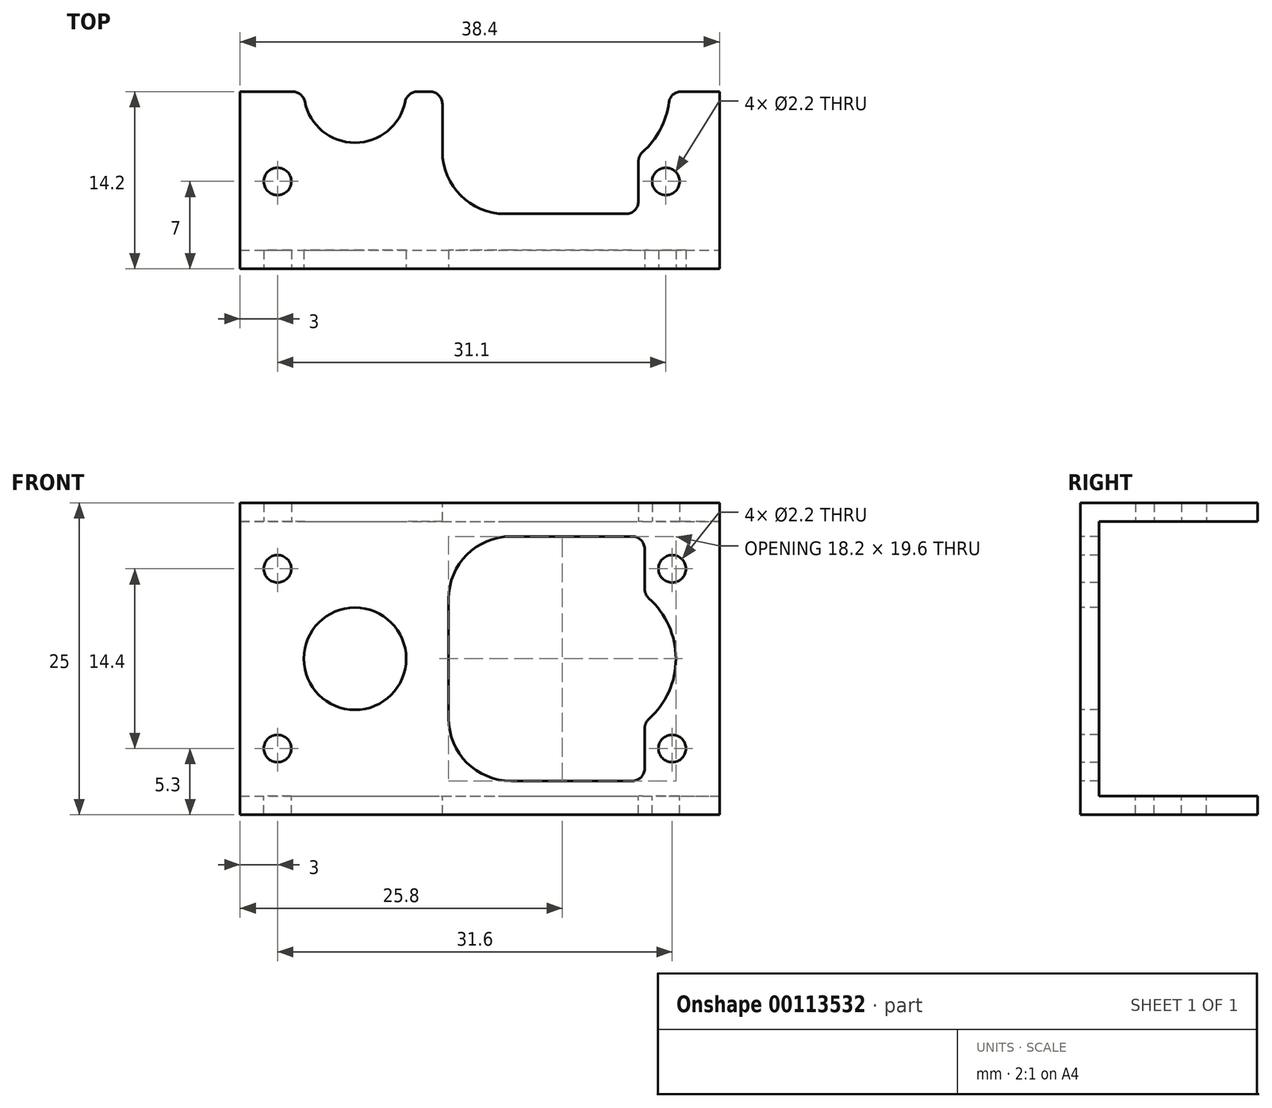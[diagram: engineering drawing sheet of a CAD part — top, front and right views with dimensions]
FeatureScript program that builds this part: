
annotation { "Feature Type Name" : "Feature", "Feature Type Description" : "" }
export const myFeature = defineFeature(function(context is Context, id is Id, definition is map)
    precondition{}
    {
        {
            var Q0;
            Q0=qCreatedBy(makeId("Top.planeOp"),FACE);
            var sketch = newSketch(context, id + "F0", { "sketchPlane" : qUnion([Q0])});
            skLineSegment(sketch, "E0.bottom", {"start": v(19.2, -14.2) * mm, "end": v(-19.2, -14.2) * mm});
            skLineSegment(sketch, "E0.top", {"start": v(19.2, 14.2) * mm, "end": v(-19.2, 14.2) * mm});
            skLineSegment(sketch, "E0.left", {"start": v(19.2, -14.2) * mm, "end": v(19.2, 14.2) * mm});
            skLineSegment(sketch, "E0.right", {"start": v(-19.2, -14.2) * mm, "end": v(-19.2, 14.2) * mm});
            skPoint(sketch, "E0.middle", {"position": v(0, 0) * mm});
            skCircle(sketch, "E1", {"center": v(-10, 0) * mm, "radius": 4.1 * mm});
            skCircle(sketch, "E2", {"center": v(-16.2, 7.2) * mm, "radius": 1.1 * mm});
            skCircle(sketch, "E3", {"center": v(14.9, 7.2) * mm, "radius": 1.1 * mm});
            skLineSegment(sketch, "E4.bottom", {"start": v(2, 9.8) * mm, "end": v(11.7, 9.8) * mm});
            skLineSegment(sketch, "E4.top", {"start": v(2, -9.8) * mm, "end": v(11.7, -9.8) * mm});
            skLineSegment(sketch, "E4.left", {"start": v(-3, 4.8) * mm, "end": v(-3, -4.8) * mm});
            skLineSegment(sketch, "E4.right", {"start": v(12.7, 8.8) * mm, "end": v(12.7, 5.6) * mm});
            skPoint(sketch, "E4.middle", {"position": v(4.85, 0) * mm});
            skPoint(sketch, "E5.visualSharp", {"position": v(-3, 9.8) * mm});
            skArc(sketch, "E5.filletArc", {"start": v(2, 9.8) * mm, "mid": v(-1.54, 8.34) * mm, "end": v(-3, 4.8) * mm});
            skPoint(sketch, "E6.visualSharp", {"position": v(-3, -9.8) * mm});
            skArc(sketch, "E6.filletArc", {"start": v(-3, -4.8) * mm, "mid": v(-1.54, -8.34) * mm, "end": v(2, -9.8) * mm});
            skPoint(sketch, "E7.visualSharp", {"position": v(12.7, 9.8) * mm});
            skArc(sketch, "E7.filletArc", {"start": v(12.7, 8.8) * mm, "mid": v(12.4, 9.5) * mm, "end": v(11.7, 9.8) * mm});
            skPoint(sketch, "E8.visualSharp", {"position": v(12.7, -9.8) * mm});
            skArc(sketch, "E8.filletArc", {"start": v(11.7, -9.8) * mm, "mid": v(12.4, -9.5) * mm, "end": v(12.7, -8.8) * mm});
            skCircle(sketch, "E9.MirrorC", {"center": v(-16.2, -7.2) * mm, "radius": 1.1 * mm});
            skCircle(sketch, "E10.MirrorC", {"center": v(14.9, -7.2) * mm, "radius": 1.1 * mm});
            skArc(sketch, "E11", {"start": v(13.03, -4.84) * mm, "mid": v(15.2, 0) * mm, "end": v(13.03, 4.84) * mm});
            skLineSegment(sketch, "E12.trimOffspring", {"start": v(12.7, -5.6) * mm, "end": v(12.7, -8.8) * mm});
            skPoint(sketch, "E13.visualSharp", {"position": v(12.7, 5.12) * mm});
            skArc(sketch, "E13.filletArc", {"start": v(12.7, 5.6) * mm, "mid": v(12.79, 5.18) * mm, "end": v(13.03, 4.84) * mm});
            skPoint(sketch, "E14.visualSharp", {"position": v(12.7, -5.12) * mm});
            skArc(sketch, "E14.filletArc", {"start": v(13.03, -4.84) * mm, "mid": v(12.79, -5.18) * mm, "end": v(12.7, -5.6) * mm});
            skSolve(sketch);
        }
        {
            var Q0;
            Q0=qSketchRegion(id+"F0",true);
            extrude(context, id + "F1", {"entities" : qUnion([Q0]), "depth" : 1.5 * mm});
        }
        {
            var Q0;
            Q0=makeQuery(id+"F1.opExtrude","CAP_FACE",FACE,{"disambiguationData":[OSD([sQuery(id+"F0.wireOp",EDGE,"E0.bottom"),sQuery(id+"F0.wireOp",EDGE,"E0.top"),sQuery(id+"F0.wireOp",EDGE,"E0.left"),sQuery(id+"F0.wireOp",EDGE,"E0.right"),sQuery(id+"F0.wireOp",EDGE,"E1"),sQuery(id+"F0.wireOp",EDGE,"E2"),sQuery(id+"F0.wireOp",EDGE,"E3"),sQuery(id+"F0.wireOp",EDGE,"E4.bottom"),sQuery(id+"F0.wireOp",EDGE,"E4.top"),sQuery(id+"F0.wireOp",EDGE,"E4.left"),sQuery(id+"F0.wireOp",EDGE,"E4.right"),sQuery(id+"F0.wireOp",EDGE,"E5.filletArc"),sQuery(id+"F0.wireOp",EDGE,"E6.filletArc"),sQuery(id+"F0.wireOp",EDGE,"E7.filletArc"),sQuery(id+"F0.wireOp",EDGE,"E8.filletArc"),sQuery(id+"F0.wireOp",EDGE,"E9.MirrorC"),sQuery(id+"F0.wireOp",EDGE,"E10.MirrorC"),sQuery(id+"F0.wireOp",EDGE,"E11"),sQuery(id+"F0.wireOp",EDGE,"E12.trimOffspring"),sQuery(id+"F0.wireOp",EDGE,"E13.filletArc"),sQuery(id+"F0.wireOp",EDGE,"E14.filletArc")])],"isStart":true});
            var sketch = newSketch(context, id + "F2", { "sketchPlane" : qUnion([Q0])});
            skLineSegment(sketch, "E15.bottom", {"start": v(-19.2, 14.2) * mm, "end": v(19.2, 14.2) * mm});
            skLineSegment(sketch, "E15.top", {"start": v(-19.2, 12.7) * mm, "end": v(19.2, 12.7) * mm});
            skLineSegment(sketch, "E15.left", {"start": v(-19.2, 14.2) * mm, "end": v(-19.2, 12.7) * mm});
            skLineSegment(sketch, "E15.right", {"start": v(19.2, 14.2) * mm, "end": v(19.2, 12.7) * mm});
            skSolve(sketch);
        }
        {
            var Q0;
            Q0=qSketchRegion(id+"F2",true);
            extrude(context, id + "F3", {"entities" : qUnion([Q0]), "operationType" : NewBodyOperationType.ADD, "depth" : 11 * mm});
        }
        {
            var Q0;
            Q0=qCreatedBy(makeId("Top.planeOp"),FACE);
            cPlane(context, id + "F4", {"entities" : qUnion([Q0]), "cplaneType" : CPlaneType.OFFSET, "offset" : 11 * mm, "oppositeDirection" : true, "width" : 150 * mm, "height" : 150 * mm});
        }
        {
            var Q0;
            Q0=makeQuery(id+"F1.opExtrude","SWEPT_BODY",BODY,{"disambiguationData":[OSD([sQuery(id+"F0.wireOp",EDGE,"E0.bottom"),sQuery(id+"F0.wireOp",EDGE,"E0.top"),sQuery(id+"F0.wireOp",EDGE,"E0.left"),sQuery(id+"F0.wireOp",EDGE,"E0.right"),sQuery(id+"F0.wireOp",EDGE,"E1"),sQuery(id+"F0.wireOp",EDGE,"E2"),sQuery(id+"F0.wireOp",EDGE,"E3"),sQuery(id+"F0.wireOp",EDGE,"E4.bottom"),sQuery(id+"F0.wireOp",EDGE,"E4.top"),sQuery(id+"F0.wireOp",EDGE,"E4.left"),sQuery(id+"F0.wireOp",EDGE,"E4.right"),sQuery(id+"F0.wireOp",EDGE,"E5.filletArc"),sQuery(id+"F0.wireOp",EDGE,"E6.filletArc"),sQuery(id+"F0.wireOp",EDGE,"E7.filletArc"),sQuery(id+"F0.wireOp",EDGE,"E8.filletArc"),sQuery(id+"F0.wireOp",EDGE,"E9.MirrorC"),sQuery(id+"F0.wireOp",EDGE,"E10.MirrorC"),sQuery(id+"F0.wireOp",EDGE,"E11"),sQuery(id+"F0.wireOp",EDGE,"E12.trimOffspring"),sQuery(id+"F0.wireOp",EDGE,"E13.filletArc"),sQuery(id+"F0.wireOp",EDGE,"E14.filletArc")])]});
            var Q1;
            Q1=qCreatedBy(id+"F4.planeOp",FACE);
            mirror(context, id + "F5", {"operationType" : NewBodyOperationType.ADD, "entities" : qUnion([Q0]), "mirrorPlane" : qUnion([Q1])});
        }
        {
            var Q0;
            Q0=makeQuery(id+"F5.opPattern","COPY",FACE,{"derivedFrom":makeQuery(id+"F1.opExtrude","CAP_FACE",FACE,{"disambiguationData":[OSD([sQuery(id+"F0.wireOp",EDGE,"E0.bottom"),sQuery(id+"F0.wireOp",EDGE,"E0.top"),sQuery(id+"F0.wireOp",EDGE,"E0.left"),sQuery(id+"F0.wireOp",EDGE,"E0.right"),sQuery(id+"F0.wireOp",EDGE,"E1"),sQuery(id+"F0.wireOp",EDGE,"E2"),sQuery(id+"F0.wireOp",EDGE,"E3"),sQuery(id+"F0.wireOp",EDGE,"E4.bottom"),sQuery(id+"F0.wireOp",EDGE,"E4.top"),sQuery(id+"F0.wireOp",EDGE,"E4.left"),sQuery(id+"F0.wireOp",EDGE,"E4.right"),sQuery(id+"F0.wireOp",EDGE,"E5.filletArc"),sQuery(id+"F0.wireOp",EDGE,"E6.filletArc"),sQuery(id+"F0.wireOp",EDGE,"E7.filletArc"),sQuery(id+"F0.wireOp",EDGE,"E8.filletArc"),sQuery(id+"F0.wireOp",EDGE,"E9.MirrorC"),sQuery(id+"F0.wireOp",EDGE,"E10.MirrorC"),sQuery(id+"F0.wireOp",EDGE,"E11"),sQuery(id+"F0.wireOp",EDGE,"E12.trimOffspring"),sQuery(id+"F0.wireOp",EDGE,"E13.filletArc"),sQuery(id+"F0.wireOp",EDGE,"E14.filletArc")])],"isStart":false}),"instanceName":"1"});
            var sketch = newSketch(context, id + "F6", { "sketchPlane" : qUnion([Q0])});
            skLineSegment(sketch, "E16.bottom", {"start": v(-19.2, -14.2) * mm, "end": v(19.2, -14.2) * mm});
            skLineSegment(sketch, "E16.top", {"start": v(-19.2, 0) * mm, "end": v(19.2, 0) * mm});
            skLineSegment(sketch, "E16.left", {"start": v(-19.2, -14.2) * mm, "end": v(-19.2, 0) * mm});
            skLineSegment(sketch, "E16.right", {"start": v(19.2, -14.2) * mm, "end": v(19.2, 0) * mm});
            skSolve(sketch);
        }
        {
            var Q0;
            Q0=qSketchRegion(id+"F6",true);
            extrude(context, id + "F7", {"entities" : qUnion([Q0]), "operationType" : NewBodyOperationType.REMOVE, "endBound" : BoundingType.THROUGH_ALL, "oppositeDirection" : true, "depth" : 25 * mm});
        }
        {
            var Q0;
            {var subQ0=makeQuery(id+"F3.boolean.opBoolean","MERGE",FACE,{"derivedFrom":[makeQuery(id+"F1.opExtrude","SWEPT_FACE",FACE,{"disambiguationData":[OSD([sQuery(id+"F0.wireOp",EDGE,"E0.bottom")])]}),makeQuery(id+"F3.opExtrude","SWEPT_FACE",FACE,{"disambiguationData":[OSD([sQuery(id+"F2.wireOp",EDGE,"E15.bottom")])]})]});Q0=makeQuery(id+"F5.boolean.opBoolean","MERGE",FACE,{"derivedFrom":[subQ0,makeQuery(id+"F5.opPattern","COPY",FACE,{"derivedFrom":subQ0,"instanceName":"1"})]});}
            var sketch = newSketch(context, id + "F8", { "sketchPlane" : qUnion([Q0])});
            skLineSegment(sketch, "E17", {"start": v(-19.2, -11) * mm, "end": v(19.2, -11) * mm, "construction": true});
            skCircle(sketch, "E18", {"center": v(-10, -11) * mm, "radius": 4.1 * mm});
            skCircle(sketch, "E19", {"center": v(-16.2, -3.8) * mm, "radius": 1.1 * mm});
            skCircle(sketch, "E20", {"center": v(15.4, -3.8) * mm, "radius": 1.1 * mm});
            skLineSegment(sketch, "E21.bottom", {"start": v(2.5, -1.2) * mm, "end": v(12.2, -1.2) * mm});
            skLineSegment(sketch, "E21.top", {"start": v(2.5, -20.8) * mm, "end": v(12.2, -20.8) * mm});
            skLineSegment(sketch, "E21.left", {"start": v(-2.5, -6.2) * mm, "end": v(-2.5, -15.8) * mm});
            skLineSegment(sketch, "E21.right", {"start": v(13.2, -2.2) * mm, "end": v(13.2, -5.4) * mm});
            skPoint(sketch, "E21.middle", {"position": v(5.35, -11) * mm});
            skPoint(sketch, "E22.visualSharp", {"position": v(-2.5, -1.2) * mm});
            skArc(sketch, "E22.filletArc", {"start": v(2.5, -1.2) * mm, "mid": v(-1.04, -2.66) * mm, "end": v(-2.5, -6.2) * mm});
            skPoint(sketch, "E23.visualSharp", {"position": v(-2.5, -20.8) * mm});
            skArc(sketch, "E23.filletArc", {"start": v(-2.5, -15.8) * mm, "mid": v(-1.04, -19.34) * mm, "end": v(2.5, -20.8) * mm});
            skPoint(sketch, "E24.visualSharp", {"position": v(13.2, -1.2) * mm});
            skArc(sketch, "E24.filletArc", {"start": v(13.2, -2.2) * mm, "mid": v(12.9, -1.5) * mm, "end": v(12.2, -1.2) * mm});
            skPoint(sketch, "E25.visualSharp", {"position": v(13.2, -20.8) * mm});
            skArc(sketch, "E25.filletArc", {"start": v(12.2, -20.8) * mm, "mid": v(12.9, -20.5) * mm, "end": v(13.2, -19.8) * mm});
            skArc(sketch, "E26", {"start": v(13.53, -15.84) * mm, "mid": v(15.7, -11) * mm, "end": v(13.53, -6.16) * mm});
            skLineSegment(sketch, "E27.trimOffspring", {"start": v(13.2, -16.6) * mm, "end": v(13.2, -19.8) * mm});
            skPoint(sketch, "E28.visualSharp", {"position": v(13.2, -5.88) * mm});
            skArc(sketch, "E28.filletArc", {"start": v(13.2, -5.4) * mm, "mid": v(13.29, -5.82) * mm, "end": v(13.53, -6.16) * mm});
            skPoint(sketch, "E29.visualSharp", {"position": v(13.2, -16.12) * mm});
            skArc(sketch, "E29.filletArc", {"start": v(13.53, -15.84) * mm, "mid": v(13.29, -16.18) * mm, "end": v(13.2, -16.6) * mm});
            skCircle(sketch, "E30.MirrorC", {"center": v(-16.2, -18.2) * mm, "radius": 1.1 * mm});
            skCircle(sketch, "E31.MirrorC", {"center": v(15.4, -18.2) * mm, "radius": 1.1 * mm});
            skSolve(sketch);
        }
        {
            var Q0;
            Q0=qSketchRegion(id+"F8",true);
            extrude(context, id + "F9", {"entities" : qUnion([Q0]), "operationType" : NewBodyOperationType.REMOVE, "endBound" : BoundingType.UP_TO_NEXT, "oppositeDirection" : true, "depth" : 25 * mm});
        }
        {
            var Q0;
            Q0=makeQuery(id+"F7.boolean.opBoolean","COPY",EDGE,{"disambiguationData":[OD(0.0)],"derivedFrom":makeQuery(id+"F7.opExtrude","SWEPT_EDGE",EDGE,{"disambiguationData":[OSD([sQuery(id+"F0.wireOp",EDGE,"E0.right"),sQuery(id+"F6.wireOp",EDGE,"E16.top"),sQuery(id+"F6.wireOp",EDGE,"E16.left")])]})});
            var Q1;
            Q1=makeQuery(id+"F7.boolean.opBoolean","COPY",EDGE,{"disambiguationData":[OD(1.0)],"derivedFrom":makeQuery(id+"F7.opExtrude","SWEPT_EDGE",EDGE,{"disambiguationData":[OSD([sQuery(id+"F0.wireOp",EDGE,"E0.right"),sQuery(id+"F6.wireOp",EDGE,"E16.top"),sQuery(id+"F6.wireOp",EDGE,"E16.left")])]})});
            var Q2;
            Q2=makeQuery(id+"F7.boolean.opBoolean","INTERSECT",EDGE,{"disambiguationData":[OD(1.0)],"derivedFrom":[makeQuery(id+"F1.opExtrude","SWEPT_FACE",FACE,{"disambiguationData":[OSD([sQuery(id+"F0.wireOp",EDGE,"E1")])]}),makeQuery(id+"F7.opExtrude","SWEPT_FACE",FACE,{"disambiguationData":[OSD([sQuery(id+"F6.wireOp",EDGE,"E16.top")])]})]});
            var Q3;
            Q3=makeQuery(id+"F7.boolean.opBoolean","INTERSECT",EDGE,{"disambiguationData":[OD(1.0)],"derivedFrom":[makeQuery(id+"F5.opPattern","COPY",FACE,{"derivedFrom":makeQuery(id+"F1.opExtrude","SWEPT_FACE",FACE,{"disambiguationData":[OSD([sQuery(id+"F0.wireOp",EDGE,"E1")])]}),"instanceName":"1"}),makeQuery(id+"F7.opExtrude","SWEPT_FACE",FACE,{"disambiguationData":[OSD([sQuery(id+"F6.wireOp",EDGE,"E16.top")])]})]});
            var Q4;
            Q4=makeQuery(id+"F7.boolean.opBoolean","INTERSECT",EDGE,{"disambiguationData":[OD(0.0)],"derivedFrom":[makeQuery(id+"F5.opPattern","COPY",FACE,{"derivedFrom":makeQuery(id+"F1.opExtrude","SWEPT_FACE",FACE,{"disambiguationData":[OSD([sQuery(id+"F0.wireOp",EDGE,"E1")])]}),"instanceName":"1"}),makeQuery(id+"F7.opExtrude","SWEPT_FACE",FACE,{"disambiguationData":[OSD([sQuery(id+"F6.wireOp",EDGE,"E16.top")])]})]});
            var Q5;
            Q5=makeQuery(id+"F7.boolean.opBoolean","INTERSECT",EDGE,{"derivedFrom":[makeQuery(id+"F5.opPattern","COPY",FACE,{"derivedFrom":makeQuery(id+"F1.opExtrude","SWEPT_FACE",FACE,{"disambiguationData":[OSD([sQuery(id+"F0.wireOp",EDGE,"E4.left")])]}),"instanceName":"1"}),makeQuery(id+"F7.opExtrude","SWEPT_FACE",FACE,{"disambiguationData":[OSD([sQuery(id+"F6.wireOp",EDGE,"E16.top")])]})]});
            var Q6;
            Q6=makeQuery(id+"F7.boolean.opBoolean","INTERSECT",EDGE,{"disambiguationData":[OD(0.0)],"derivedFrom":[makeQuery(id+"F1.opExtrude","SWEPT_FACE",FACE,{"disambiguationData":[OSD([sQuery(id+"F0.wireOp",EDGE,"E1")])]}),makeQuery(id+"F7.opExtrude","SWEPT_FACE",FACE,{"disambiguationData":[OSD([sQuery(id+"F6.wireOp",EDGE,"E16.top")])]})]});
            var Q7;
            Q7=makeQuery(id+"F7.boolean.opBoolean","INTERSECT",EDGE,{"derivedFrom":[makeQuery(id+"F5.opPattern","COPY",FACE,{"derivedFrom":makeQuery(id+"F1.opExtrude","SWEPT_FACE",FACE,{"disambiguationData":[OSD([sQuery(id+"F0.wireOp",EDGE,"E11")])]}),"instanceName":"1"}),makeQuery(id+"F7.opExtrude","SWEPT_FACE",FACE,{"disambiguationData":[OSD([sQuery(id+"F6.wireOp",EDGE,"E16.top")])]})]});
            var Q8;
            Q8=makeQuery(id+"F7.boolean.opBoolean","INTERSECT",EDGE,{"derivedFrom":[makeQuery(id+"F1.opExtrude","SWEPT_FACE",FACE,{"disambiguationData":[OSD([sQuery(id+"F0.wireOp",EDGE,"E11")])]}),makeQuery(id+"F7.opExtrude","SWEPT_FACE",FACE,{"disambiguationData":[OSD([sQuery(id+"F6.wireOp",EDGE,"E16.top")])]})]});
            var Q9;
            Q9=makeQuery(id+"F7.boolean.opBoolean","COPY",EDGE,{"disambiguationData":[OD(0.0)],"derivedFrom":makeQuery(id+"F7.opExtrude","SWEPT_EDGE",EDGE,{"disambiguationData":[OSD([sQuery(id+"F0.wireOp",EDGE,"E0.left"),sQuery(id+"F6.wireOp",EDGE,"E16.top"),sQuery(id+"F6.wireOp",EDGE,"E16.right")])]})});
            var Q10;
            Q10=makeQuery(id+"F7.boolean.opBoolean","INTERSECT",EDGE,{"derivedFrom":[makeQuery(id+"F1.opExtrude","SWEPT_FACE",FACE,{"disambiguationData":[OSD([sQuery(id+"F0.wireOp",EDGE,"E4.left")])]}),makeQuery(id+"F7.opExtrude","SWEPT_FACE",FACE,{"disambiguationData":[OSD([sQuery(id+"F6.wireOp",EDGE,"E16.top")])]})]});
            var Q11;
            Q11=makeQuery(id+"F7.boolean.opBoolean","COPY",EDGE,{"disambiguationData":[OD(1.0)],"derivedFrom":makeQuery(id+"F7.opExtrude","SWEPT_EDGE",EDGE,{"disambiguationData":[OSD([sQuery(id+"F0.wireOp",EDGE,"E0.left"),sQuery(id+"F6.wireOp",EDGE,"E16.top"),sQuery(id+"F6.wireOp",EDGE,"E16.right")])]})});
            fillet(context, id + "F10", {"entities" : qUnion([Q0, Q1, Q2, Q3, Q4, Q5, Q6, Q7, Q8, Q9, Q10, Q11]), "radius" : 1 * mm, "tangentPropagation" : true, "allowEdgeOverflow" : false});
        }
    });
